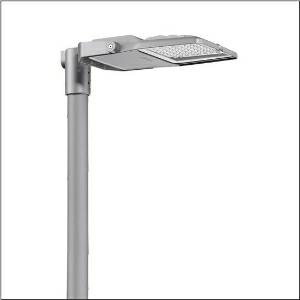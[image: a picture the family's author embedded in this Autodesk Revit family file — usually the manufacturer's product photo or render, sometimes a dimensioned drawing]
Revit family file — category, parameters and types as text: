
# Revit family: floodlight_fl_21_mini___pl43_5xa7776c4a3a_ef43
name_source: partatom
category: Lighting Fixtures
units: mm (PartAtom-declared; Revit-internal decimal feet)

## family parameters
Cut with Voids When Loaded = No
Host = Face
Light Source = No
Part Type = Normal
Room Calculation Point = No
Round Connector Dimension = Use Diameter
Shared = No

## types (1)
- --- (1 x LED, 13020 lm, 89 W, 4000K)
    Apparent Load = 89 VA
    CIE Flux Codes = 27 78 99 100 100
    Color Rendering = 70
    Color Temperature = 4000K
    Default Elevation = 1800 mm
    Description = Floodlight FL 21 mini, floodlight, primary light control with lens, of PMMA, primary optical cover: protective disc, of toughened safety glass, transparent, light distribution: PL43, light emission: direct distribution, installation type: surface-mounted, LED, High Power LED, rated luminous flux: 13.020lm, luminous efficacy: 146lm/W, light colour: 740, colour temperature: 4000K, control gear: Smart Interface (Zhaga), control: pre-setting: logarithmic dimming characteristic, flexible luminous flux parameterisation, time-dependent luminous flux control, constant luminous flux control, overheat protection, with terminal, 6-pole, mains connection: 220..240V, AC, 50/60Hz, start of lifetime: 89W, end of service life: 94W, reduction: 43W, luminaire housing, of diecast aluminium, powder-coated, Siteco® metallic grey (DB 702S), corrosivity category C5 mid according to DIN EN ISO 12944, suitable for swimming pools, chlorine-resistant, sealing non-destructively replaceable, please order mast flange separately, mast bracket, of steel, galvanised, powder-coated, Siteco® metallic grey (DB 702S), Smart Interface below and above, protection rating (complete): IP66, insulation class (complete): insulation class II (safety insulation), certification: CE, ENEC, VDE, protection symbol: D, impact resistance: IK08, permissible operating ambient temperature: -40..+40°C, permissible operating ambient temperature for outdoor applications: -40..+50°C, standard: DIN EN 12944, LABS conformity tested according to VDMA 24364:2018-05, packaging unit: 1 piece

Light Distribution: PL43
    Height = 70 mm
    Lamp = 1 x LED
    Lamp Light Flux = 13020 lm
    Lamp Power = 89 W
    Lamp count = 1
    Length = 485 mm
    Luminous efficacy = 146 lm/W
    Manufacturer = Siteco
    ModVariant = No
    Model = 5XA7776C4A3A
    Number of Poles = 1
    OnlyDefault = Yes
    Power Factor = 1
    Product Name = Floodlight FL 21 mini | PL43
    Product group = floodlight | pylon annexe
    ProductGroupID = 6201
    Protection Class = Protection class II
    Protection Degree = IP 66
    RLX_Detail_Level = 1
    RLX_Emergency_Light_Flux = 0 lm
    RLX_Emergency_Type = 0
    RLX_Emergency_Type_DB = No
    RlxData = <blob elided: 100969 chars, md5=19ba0c16>
    Socket = socket
    Standby Power = 0 W
    System Light Flux = 13020 lm
    System Power = 89 W
    Type Comments = factory setting: luminous flux: 100 % | dim-lin: 254 | 456 mA
    Type Image = l_1007125.jpg
    URL = http://relux.com
    VarID = @adj_116829
    Voltage = 0 V
    Weight = 0.00 kg
    Width = 337 mm

## geometry (parser evidence)
native form markers: Blend x4, Sweep x11
no freeform markers — native parametric forms only
